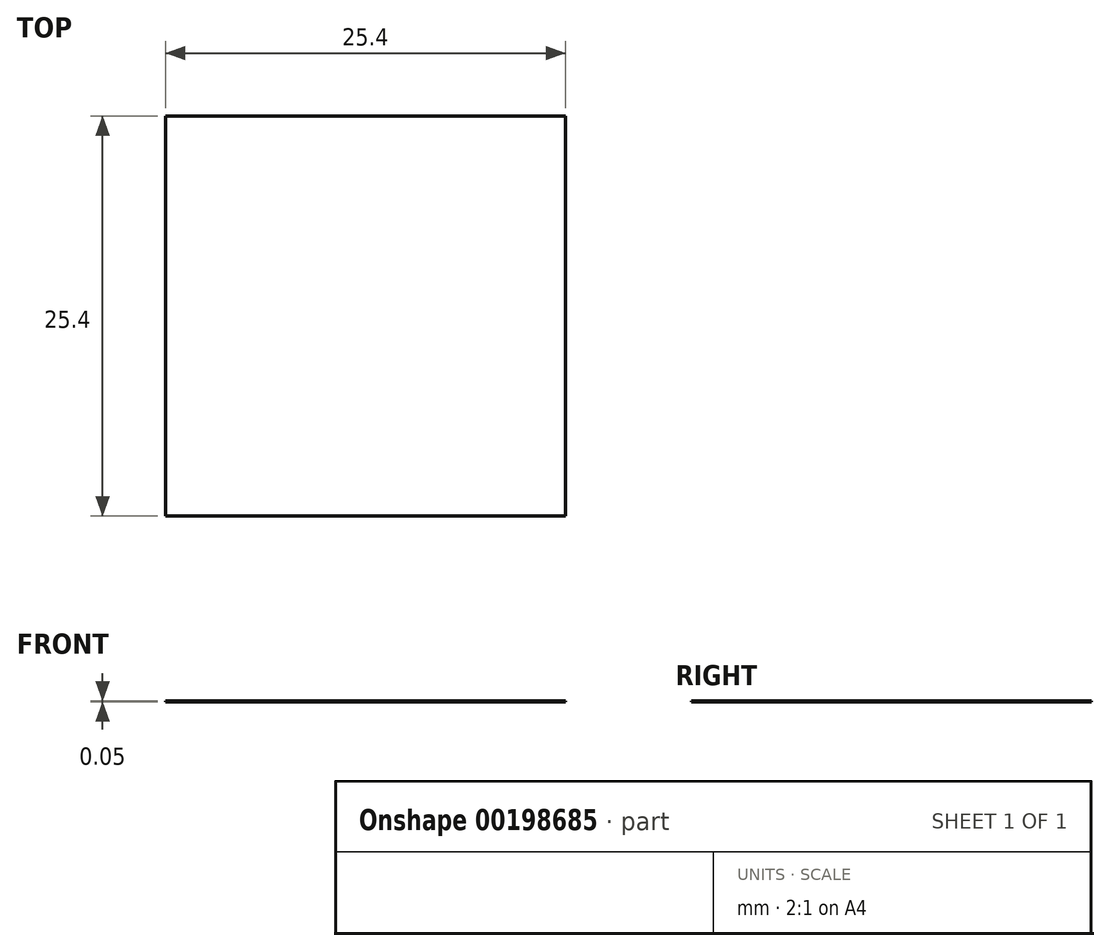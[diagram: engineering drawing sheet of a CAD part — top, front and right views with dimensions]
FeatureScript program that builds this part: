
annotation { "Feature Type Name" : "Feature", "Feature Type Description" : "" }
export const myFeature = defineFeature(function(context is Context, id is Id, definition is map)
    precondition{}
    {
        {
            var Q0;
            Q0=qCreatedBy(makeId("Top.planeOp"),FACE);
            var sketch = newSketch(context, id + "F0", { "sketchPlane" : qUnion([Q0])});
            skLineSegment(sketch, "E0.bottom", {"start": v(12.7, -12.7) * mm, "end": v(-12.7, -12.7) * mm});
            skLineSegment(sketch, "E0.top", {"start": v(12.7, 12.7) * mm, "end": v(-12.7, 12.7) * mm});
            skLineSegment(sketch, "E0.left", {"start": v(12.7, -12.7) * mm, "end": v(12.7, 12.7) * mm});
            skLineSegment(sketch, "E0.right", {"start": v(-12.7, -12.7) * mm, "end": v(-12.7, 12.7) * mm});
            skPoint(sketch, "E0.middle", {"position": v(0, 0) * mm});
            skSolve(sketch);
        }
        {
            var Q0;
            Q0 = qSketchRegion(id + "F0", true);
            extrude(context, id + "F1", {"entities" : qUnion([Q0]), "depth" : 0.05 * mm});
        }
    });
